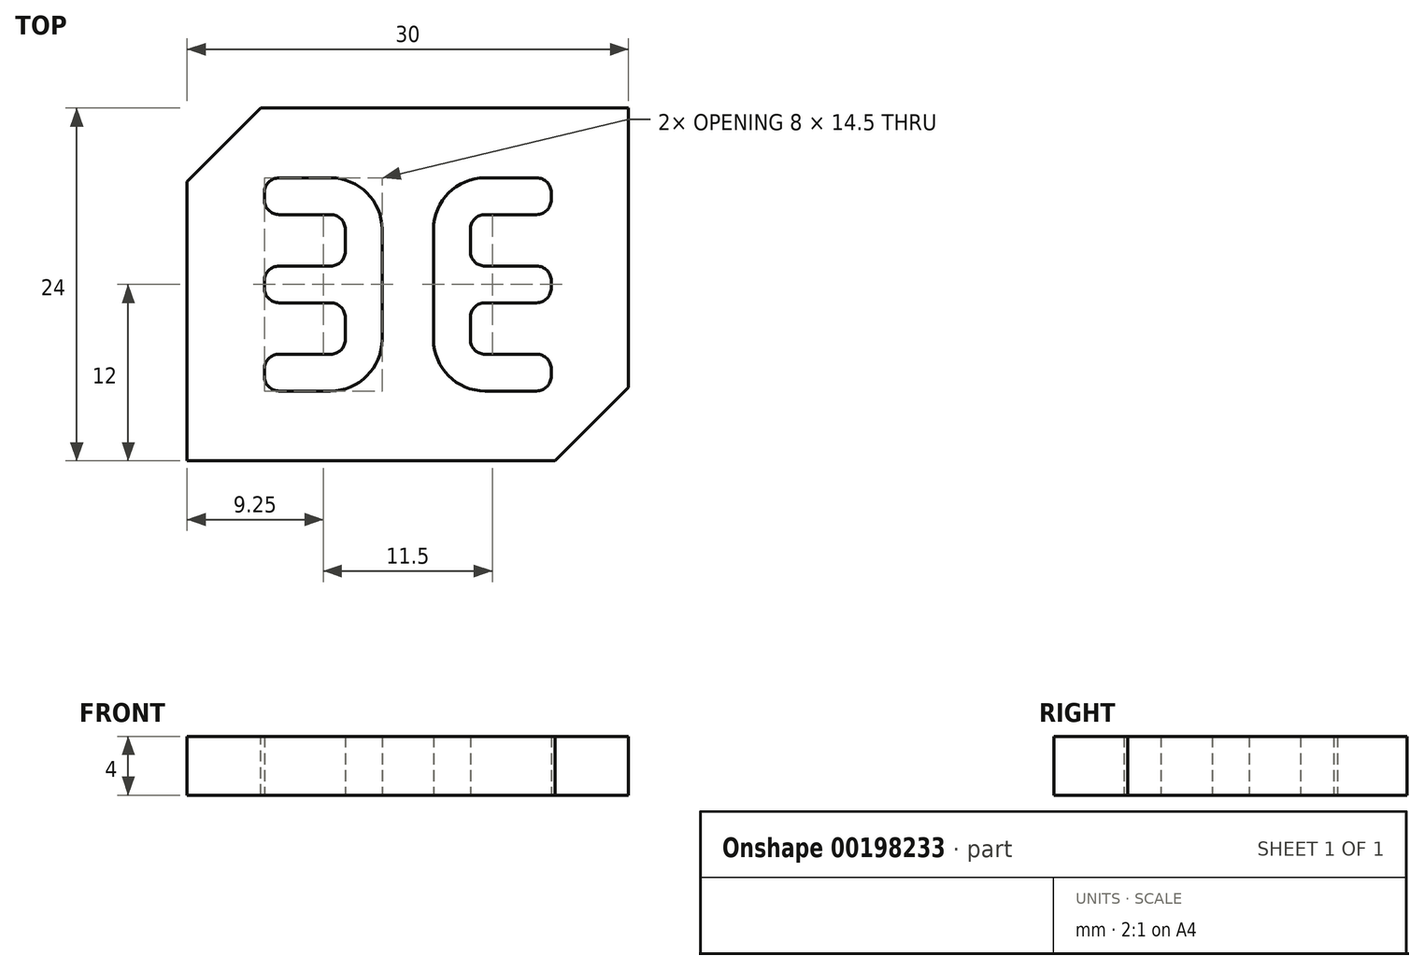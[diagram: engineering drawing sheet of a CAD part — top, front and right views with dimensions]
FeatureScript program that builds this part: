
annotation { "Feature Type Name" : "Feature", "Feature Type Description" : "" }
export const myFeature = defineFeature(function(context is Context, id is Id, definition is map)
    precondition{}
    {
        {
            var Q0;
            Q0=qCreatedBy(makeId("Top.planeOp"),FACE);
            var sketch = newSketch(context, id + "F0", { "sketchPlane" : qUnion([Q0])});
            skLineSegment(sketch, "E0.bottom", {"start": v(5.25, 7.25) * mm, "end": v(8.75, 7.25) * mm});
            skLineSegment(sketch, "E0.top", {"start": v(5.25, -7.25) * mm, "end": v(8.75, -7.25) * mm});
            skLineSegment(sketch, "E0.left", {"start": v(1.75, 3.75) * mm, "end": v(1.75, -3.75) * mm});
            skLineSegment(sketch, "E0.right", {"start": v(9.75, 6.25) * mm, "end": v(9.75, 5.75) * mm});
            skLineSegment(sketch, "E1.bottom", {"start": v(5.25, 4.75) * mm, "end": v(8.75, 4.75) * mm});
            skLineSegment(sketch, "E1.top", {"start": v(5.25, 1.25) * mm, "end": v(8.75, 1.25) * mm});
            skLineSegment(sketch, "E1.left", {"start": v(4.25, 3.75) * mm, "end": v(4.25, 2.25) * mm});
            skLineSegment(sketch, "E2.bottom", {"start": v(5.25, -1.25) * mm, "end": v(8.75, -1.25) * mm});
            skLineSegment(sketch, "E2.top", {"start": v(5.25, -4.75) * mm, "end": v(8.75, -4.75) * mm});
            skLineSegment(sketch, "E2.left", {"start": v(4.25, -2.25) * mm, "end": v(4.25, -3.75) * mm});
            skLineSegment(sketch, "E3.trimOffspring", {"start": v(9.75, 0.25) * mm, "end": v(9.75, -0.25) * mm});
            skLineSegment(sketch, "E4.trimOffspring", {"start": v(9.75, -5.75) * mm, "end": v(9.75, -6.25) * mm});
            skLineSegment(sketch, "E5.MirrorCS", {"start": v(-5.25, 1.25) * mm, "end": v(-8.75, 1.25) * mm});
            skLineSegment(sketch, "E6.MirrorCS", {"start": v(-5.25, 4.75) * mm, "end": v(-8.75, 4.75) * mm});
            skLineSegment(sketch, "E7.MirrorCS", {"start": v(-4.25, -2.25) * mm, "end": v(-4.25, -3.75) * mm});
            skLineSegment(sketch, "E8.MirrorCS", {"start": v(-5.25, -4.75) * mm, "end": v(-8.75, -4.75) * mm});
            skLineSegment(sketch, "E9.MirrorCS", {"start": v(-9.75, 6.25) * mm, "end": v(-9.75, 5.75) * mm});
            skLineSegment(sketch, "E10.MirrorCS", {"start": v(-9.75, -5.75) * mm, "end": v(-9.75, -6.25) * mm});
            skLineSegment(sketch, "E11.MirrorCS", {"start": v(-5.25, 7.25) * mm, "end": v(-8.75, 7.25) * mm});
            skLineSegment(sketch, "E12.MirrorCS", {"start": v(-1.75, 3.75) * mm, "end": v(-1.75, -3.75) * mm});
            skLineSegment(sketch, "E13.MirrorCS", {"start": v(-5.25, -7.25) * mm, "end": v(-8.75, -7.25) * mm});
            skLineSegment(sketch, "E14.MirrorCS", {"start": v(-9.75, 0.25) * mm, "end": v(-9.75, -0.25) * mm});
            skLineSegment(sketch, "E15.MirrorCS", {"start": v(-5.25, -1.25) * mm, "end": v(-8.75, -1.25) * mm});
            skLineSegment(sketch, "E16.MirrorCS", {"start": v(-4.25, 3.75) * mm, "end": v(-4.25, 2.25) * mm});
            skPoint(sketch, "E17.visualSharp", {"position": v(-9.75, 7.25) * mm});
            skArc(sketch, "E17.filletArc", {"start": v(-8.75, 7.25) * mm, "mid": v(-9.46, 6.96) * mm, "end": v(-9.75, 6.25) * mm});
            skPoint(sketch, "E18.visualSharp", {"position": v(-9.75, 4.75) * mm});
            skArc(sketch, "E18.filletArc", {"start": v(-9.75, 5.75) * mm, "mid": v(-9.46, 5.04) * mm, "end": v(-8.75, 4.75) * mm});
            skPoint(sketch, "E19.visualSharp", {"position": v(-1.75, 7.25) * mm});
            skArc(sketch, "E19.filletArc", {"start": v(-1.75, 3.75) * mm, "mid": v(-2.78, 6.22) * mm, "end": v(-5.25, 7.25) * mm});
            skPoint(sketch, "E20.visualSharp", {"position": v(-9.75, 1.25) * mm});
            skArc(sketch, "E20.filletArc", {"start": v(-8.75, 1.25) * mm, "mid": v(-9.46, 0.96) * mm, "end": v(-9.75, 0.25) * mm});
            skPoint(sketch, "E21.visualSharp", {"position": v(-9.75, -1.25) * mm});
            skArc(sketch, "E21.filletArc", {"start": v(-9.75, -0.25) * mm, "mid": v(-9.46, -0.96) * mm, "end": v(-8.75, -1.25) * mm});
            skPoint(sketch, "E22.visualSharp", {"position": v(-9.75, -4.75) * mm});
            skArc(sketch, "E22.filletArc", {"start": v(-8.75, -4.75) * mm, "mid": v(-9.46, -5.04) * mm, "end": v(-9.75, -5.75) * mm});
            skPoint(sketch, "E23.visualSharp", {"position": v(-9.75, -7.25) * mm});
            skArc(sketch, "E23.filletArc", {"start": v(-9.75, -6.25) * mm, "mid": v(-9.46, -6.96) * mm, "end": v(-8.75, -7.25) * mm});
            skPoint(sketch, "E24.visualSharp", {"position": v(-1.75, -7.25) * mm});
            skArc(sketch, "E24.filletArc", {"start": v(-5.25, -7.25) * mm, "mid": v(-2.78, -6.22) * mm, "end": v(-1.75, -3.75) * mm});
            skPoint(sketch, "E25.visualSharp", {"position": v(-4.25, -4.75) * mm});
            skArc(sketch, "E25.filletArc", {"start": v(-5.25, -4.75) * mm, "mid": v(-4.54, -4.46) * mm, "end": v(-4.25, -3.75) * mm});
            skPoint(sketch, "E26.visualSharp", {"position": v(-4.25, -1.25) * mm});
            skArc(sketch, "E26.filletArc", {"start": v(-4.25, -2.25) * mm, "mid": v(-4.54, -1.54) * mm, "end": v(-5.25, -1.25) * mm});
            skPoint(sketch, "E27.visualSharp", {"position": v(-4.25, 1.25) * mm});
            skArc(sketch, "E27.filletArc", {"start": v(-5.25, 1.25) * mm, "mid": v(-4.54, 1.54) * mm, "end": v(-4.25, 2.25) * mm});
            skPoint(sketch, "E28.visualSharp", {"position": v(-4.25, 4.75) * mm});
            skArc(sketch, "E28.filletArc", {"start": v(-4.25, 3.75) * mm, "mid": v(-4.54, 4.46) * mm, "end": v(-5.25, 4.75) * mm});
            skPoint(sketch, "E29.visualSharp", {"position": v(4.25, 4.75) * mm});
            skArc(sketch, "E29.filletArc", {"start": v(5.25, 4.75) * mm, "mid": v(4.54, 4.46) * mm, "end": v(4.25, 3.75) * mm});
            skPoint(sketch, "E30.visualSharp", {"position": v(4.25, 1.25) * mm});
            skArc(sketch, "E30.filletArc", {"start": v(4.25, 2.25) * mm, "mid": v(4.54, 1.54) * mm, "end": v(5.25, 1.25) * mm});
            skPoint(sketch, "E31.visualSharp", {"position": v(4.25, -1.25) * mm});
            skArc(sketch, "E31.filletArc", {"start": v(5.25, -1.25) * mm, "mid": v(4.54, -1.54) * mm, "end": v(4.25, -2.25) * mm});
            skPoint(sketch, "E32.visualSharp", {"position": v(4.25, -4.75) * mm});
            skArc(sketch, "E32.filletArc", {"start": v(4.25, -3.75) * mm, "mid": v(4.54, -4.46) * mm, "end": v(5.25, -4.75) * mm});
            skPoint(sketch, "E33.visualSharp", {"position": v(9.75, -4.75) * mm});
            skArc(sketch, "E33.filletArc", {"start": v(9.75, -5.75) * mm, "mid": v(9.46, -5.04) * mm, "end": v(8.75, -4.75) * mm});
            skPoint(sketch, "E34.visualSharp", {"position": v(9.75, -1.25) * mm});
            skArc(sketch, "E34.filletArc", {"start": v(8.75, -1.25) * mm, "mid": v(9.46, -0.96) * mm, "end": v(9.75, -0.25) * mm});
            skPoint(sketch, "E35.visualSharp", {"position": v(9.75, 1.25) * mm});
            skArc(sketch, "E35.filletArc", {"start": v(9.75, 0.25) * mm, "mid": v(9.46, 0.96) * mm, "end": v(8.75, 1.25) * mm});
            skPoint(sketch, "E36.visualSharp", {"position": v(9.75, 4.75) * mm});
            skArc(sketch, "E36.filletArc", {"start": v(8.75, 4.75) * mm, "mid": v(9.46, 5.04) * mm, "end": v(9.75, 5.75) * mm});
            skPoint(sketch, "E37.visualSharp", {"position": v(9.75, 7.25) * mm});
            skArc(sketch, "E37.filletArc", {"start": v(9.75, 6.25) * mm, "mid": v(9.46, 6.96) * mm, "end": v(8.75, 7.25) * mm});
            skPoint(sketch, "E38.visualSharp", {"position": v(9.75, -7.25) * mm});
            skArc(sketch, "E38.filletArc", {"start": v(8.75, -7.25) * mm, "mid": v(9.46, -6.96) * mm, "end": v(9.75, -6.25) * mm});
            skPoint(sketch, "E39.visualSharp", {"position": v(1.75, -7.25) * mm});
            skArc(sketch, "E39.filletArc", {"start": v(1.75, -3.75) * mm, "mid": v(2.78, -6.22) * mm, "end": v(5.25, -7.25) * mm});
            skPoint(sketch, "E40.visualSharp", {"position": v(1.75, 7.25) * mm});
            skArc(sketch, "E40.filletArc", {"start": v(5.25, 7.25) * mm, "mid": v(2.78, 6.22) * mm, "end": v(1.75, 3.75) * mm});
            skLineSegment(sketch, "E41.bottom", {"start": v(-15, 12) * mm, "end": v(15, 12) * mm});
            skLineSegment(sketch, "E41.top", {"start": v(-15, -12) * mm, "end": v(15, -12) * mm});
            skLineSegment(sketch, "E41.left", {"start": v(-15, 12) * mm, "end": v(-15, -12) * mm});
            skLineSegment(sketch, "E41.right", {"start": v(15, 12) * mm, "end": v(15, -12) * mm});
            skSolve(sketch);
        }
        {
            var Q0;
            Q0=qSketchRegion(id+"F0",true);
            extrude(context, id + "F1", {"entities" : qUnion([Q0]), "depth" : 4 * mm});
        }
        {
            var Q0;
            Q0=makeQuery(id+"F1.opExtrude","SWEPT_EDGE",EDGE,{"disambiguationData":[OSD([sQuery(id+"F0.wireOp",EDGE,"E41.bottom"),sQuery(id+"F0.wireOp",EDGE,"E41.left")])]});
            chamfer(context, id + "F2", {"entities" : qUnion([Q0]), "width" : 5 * mm, "tangentPropagation" : true});
        }
        {
            var Q0;
            Q0=makeQuery(id+"F1.opExtrude","SWEPT_EDGE",EDGE,{"disambiguationData":[OSD([sQuery(id+"F0.wireOp",EDGE,"E41.top"),sQuery(id+"F0.wireOp",EDGE,"E41.right")])]});
            chamfer(context, id + "F3", {"entities" : qUnion([Q0]), "width" : 5 * mm, "tangentPropagation" : true});
        }
    });
